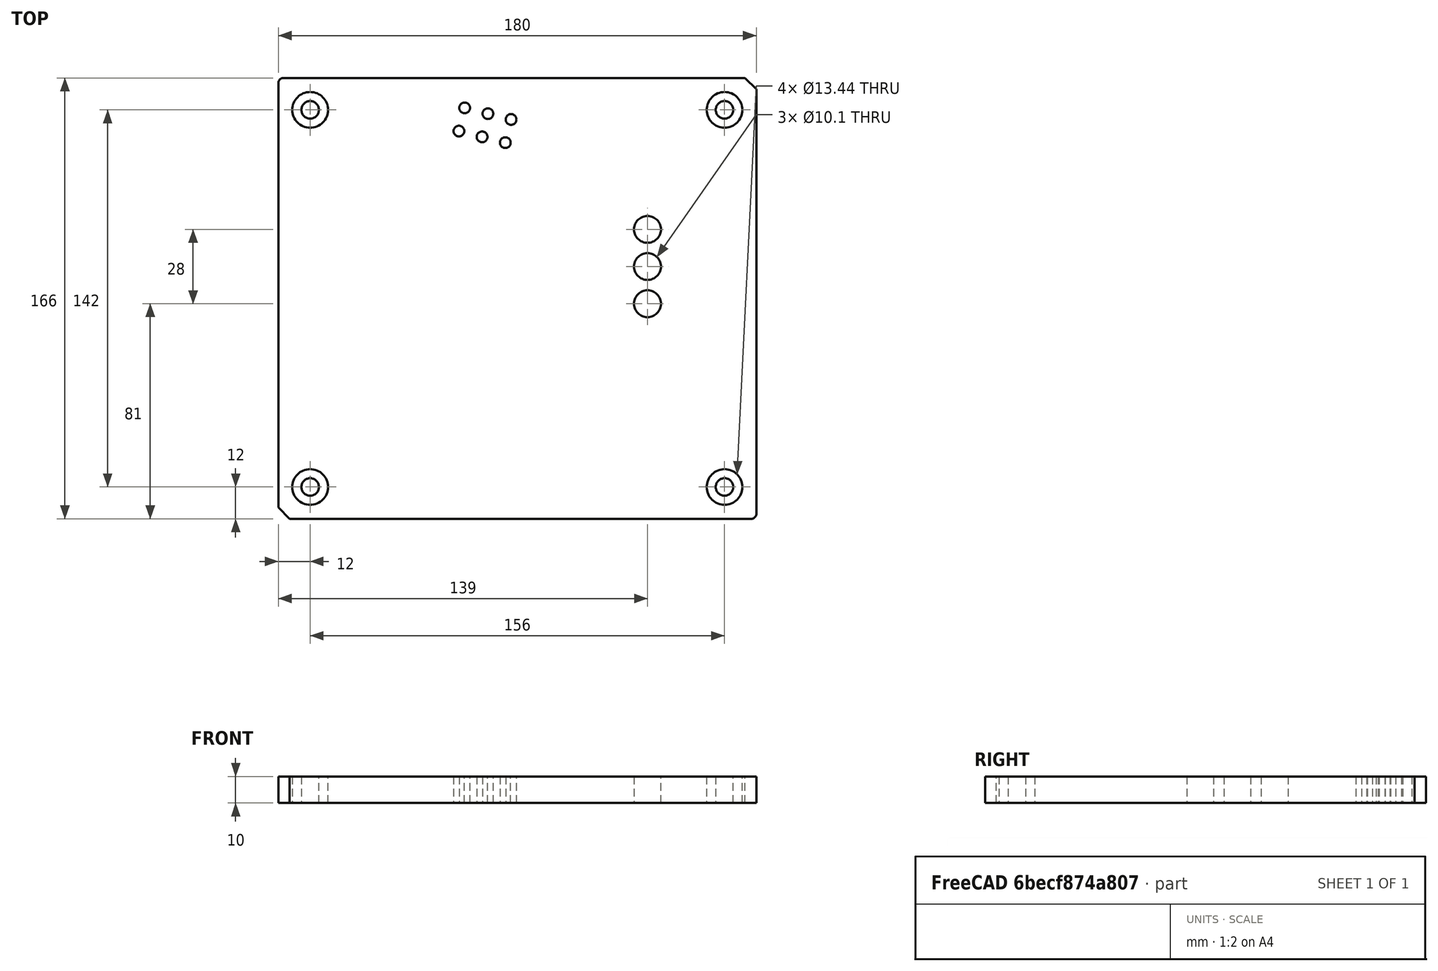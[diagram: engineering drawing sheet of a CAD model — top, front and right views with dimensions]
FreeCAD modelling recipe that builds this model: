
FCSTD DOCUMENT  (FreeCAD 0.19R24348 (Git))
Label: hopefully3d
License: All rights reserved
LicenseURL: http://en.wikipedia.org/wiki/All_rights_reserved
objects: Sketcher::SketchObject×2, Spreadsheet::Sheet×1, Part::Extrusion×1
note: 3 computed .brp shape members not serialized (recipe doc carries the construction recipe); baked Part::Feature solids carry a one-line shape summary decoded from their .brp

FEATURE [Spreadsheet::Sheet] Spreadsheet001  label="Parameters"
  cells = A1=D_1; B1(D_1)=27; A2=KAT; B2(KAT)=14; A3=KAT_2; B3(KAT_2)=28; A4=KPX; B4(KPX)=69; A5=KPY; B5(KPY)=45; A6=D_2; B6(D_2)=39; A7=RKK_1; B7(RKK_1)=6; A8=KOX; B8(KOX)=53; A9=KOY; B9(KOY)=53; A10=WX_1; B10(WX_1)=106; A11=WX_2; B11(WX_2)=136; A12=WY_1; B12(WY_1)=106; A13=RW_1; B13(RW_1)=6; A14=RW_2; B14(RW_2)=14; A15=RW_3; B15(RW_3)=27; A16=RW_4; B16(RW_4)=6; A17=RW_5; B17(RW_5)=6; A18=RW_6; B18(RW_6)=13; A19=FW_1; B19(FW_1)=6; A20=FW_2; B20(FW_2)=5.5; A21=KX_1; B21(KX_1)=12; A22=KX_2; B22(KX_2)=17; A23=KX_3; B23(KX_3)=68; A24=KX_4; B24(KX_4)=139; A25=KX_5; B25(KX_5)=168; A26=KX_6; B26(KX_6)=180; A27=KY_1; B27(KY_1)=12; A28=KY_2; B28(KY_2)=38; A29=KY_3; B29(KY_3)=109; A30=KY_4; B30(KY_4)=146; A31=KY_5; B31(KY_5)=154; A32=KY_6; B32(KY_6)=166; A33=FK_1; B33(FK_1)=2; A34=RK_1; B34(RK_1)=2; A35=H_1; B35(H_1)=12; A36=H_2; B36(H_2)=18; A37=KH_1; B37(KH_1)=10; A38=KH_2; B38(KH_2)=6; A39=OTWX_1; B39(OTWX_1)=9; A40=OTWY_1; B40(OTWY_1)=7; A41=OTWY_2; B41(OTWY_2)=14; A42=GOTW_1; B42(GOTW_1)=14; A43=GOTW_2; B43(GOTW_2)=10; A44=WY_1_1; B44(WY_1_1)=19.0787840283389
FEATURE [Sketcher::SketchObject] Sketch  label="MainFrame"
  FullyConstrained = true
  expr: Constraints[26] = <<Parameters>>.KX_1
  expr: Constraints[29] = <<Parameters>>.KY_6 - <<Parameters>>.KY_5
  expr: Constraints[10] = <<Parameters>>.KY_6
  expr: Constraints[27] = <<Parameters>>.KX_6 - <<Parameters>>.KX_5
  expr: Constraints[9] = <<Parameters>>.KX_6
  expr: Constraints[113] = <<Parameters>>.KAT
  expr: Constraints[47] = <<Parameters>>.FW_1
  expr: Constraints[67] = <<Parameters>>.KX_4
  expr: Constraints[111] = <<Parameters>>.KX_3
  expr: Constraints[68] = <<Parameters>>.KY_3
  expr: Constraints[48] = <<Parameters>>.RK_1
  expr: Constraints[81] = <<Parameters>>.OTWX_1
  expr: Constraints[28] = <<Parameters>>.KY_1
  expr: Constraints[65] = <<Parameters>>.OTWY_2
  expr: Constraints[112] = <<Parameters>>.KY_4
  expr: Constraints[80] = <<Parameters>>.OTWX_1
  sketch-geometry (49):
    g0: LineSegment StartX=0 StartY=0 StartZ=0 EndX=180 EndY=0 EndZ=0
    g1: LineSegment StartX=180 StartY=0 StartZ=0 EndX=180 EndY=166 EndZ=0
    g2: LineSegment StartX=180 StartY=166 StartZ=0 EndX=0 EndY=166 EndZ=0
    g3: LineSegment StartX=0 StartY=166 StartZ=0 EndX=0 EndY=0 EndZ=0
    g4: Circle CenterX=12 CenterY=154 CenterZ=0 NormalX=0 NormalY=0 NormalZ=1 AngleXU=0 Radius=3.3
    g5: Circle CenterX=168 CenterY=154 CenterZ=0 NormalX=0 NormalY=0 NormalZ=1 AngleXU=0 Radius=3.3
    g6: Circle CenterX=168 CenterY=12 CenterZ=0 NormalX=0 NormalY=0 NormalZ=1 AngleXU=0 Radius=3.3
    g7: Circle CenterX=12 CenterY=12 CenterZ=0 NormalX=0 NormalY=0 NormalZ=1 AngleXU=0 Radius=3.3
    g8: LineSegment StartX=12 StartY=154 StartZ=0 EndX=12 EndY=12 EndZ=0
    g9: LineSegment StartX=168 StartY=154 StartZ=0 EndX=12 EndY=154 EndZ=0
    g10: LineSegment StartX=168 StartY=12 StartZ=0 EndX=12 EndY=12 EndZ=0
    g11: LineSegment StartX=168 StartY=154 StartZ=0 EndX=168 EndY=12 EndZ=0
    g12: Circle CenterX=12 CenterY=154 CenterZ=0 NormalX=0 NormalY=0 NormalZ=1 AngleXU=0 Radius=6.72
    g13: Circle CenterX=168 CenterY=154 CenterZ=0 NormalX=0 NormalY=0 NormalZ=1 AngleXU=0 Radius=6.72
    g14: Circle CenterX=168 CenterY=12 CenterZ=0 NormalX=0 NormalY=0 NormalZ=1 AngleXU=0 Radius=6.72
    g15: Circle CenterX=12 CenterY=12 CenterZ=0 NormalX=0 NormalY=0 NormalZ=1 AngleXU=0 Radius=6.72
    g16: ArcOfCircle CenterX=2 CenterY=164 CenterZ=0 NormalX=0 NormalY=0 NormalZ=1 AngleXU=0 Radius=2 StartAngle=1.5708 EndAngle=3.14159
    g17: ArcOfCircle CenterX=178 CenterY=2 CenterZ=0 NormalX=0 NormalY=0 NormalZ=1 AngleXU=0 Radius=2 StartAngle=4.71239 EndAngle=6.28319
    g18: LineSegment StartX=0 StartY=4.24264 StartZ=0 EndX=4.24264 EndY=0 EndZ=0
    g19: LineSegment StartX=175.757 StartY=166 StartZ=0 EndX=180 EndY=161.757 EndZ=0
    g20: LineSegment StartX=0 StartY=4.24264 StartZ=0 EndX=0 EndY=164 EndZ=0
    g21: LineSegment StartX=175.757 StartY=166 StartZ=0 EndX=2 EndY=166 EndZ=0
    g22: LineSegment StartX=180 StartY=161.757 StartZ=0 EndX=180 EndY=2 EndZ=0
    g23: LineSegment StartX=4.24264 StartY=0 StartZ=0 EndX=178 EndY=0 EndZ=0
    g24: Circle CenterX=139 CenterY=109 CenterZ=0 NormalX=0 NormalY=0 NormalZ=1 AngleXU=0 Radius=5.05
    g25: LineSegment StartX=0 StartY=0 StartZ=0 EndX=139 EndY=0 EndZ=0
    g26: Circle CenterX=139 CenterY=95 CenterZ=0 NormalX=0 NormalY=0 NormalZ=1 AngleXU=0 Radius=5.05
    g27: Circle CenterX=139 CenterY=81 CenterZ=0 NormalX=0 NormalY=0 NormalZ=1 AngleXU=0 Radius=5.05
    g28: Circle CenterX=70.1773 CenterY=154.733 CenterZ=0 NormalX=0 NormalY=0 NormalZ=1 AngleXU=0 Radius=2.025
    g29: Circle CenterX=78.91 CenterY=152.555 CenterZ=0 NormalX=0 NormalY=0 NormalZ=1 AngleXU=0 Radius=2.025
    g30: Circle CenterX=87.6426 CenterY=150.378 CenterZ=0 NormalX=0 NormalY=0 NormalZ=1 AngleXU=0 Radius=2.025
    g31: Circle CenterX=68 CenterY=146 CenterZ=0 NormalX=0 NormalY=0 NormalZ=1 AngleXU=0 Radius=2.025
    g32: Circle CenterX=76.7327 CenterY=143.823 CenterZ=0 NormalX=0 NormalY=0 NormalZ=1 AngleXU=0 Radius=2.025
    g33: Circle CenterX=85.4653 CenterY=141.645 CenterZ=0 NormalX=0 NormalY=0 NormalZ=1 AngleXU=0 Radius=2.025
    g34: LineSegment StartX=85.4653 StartY=141.645 StartZ=0 EndX=87.6426 EndY=150.378 EndZ=0
    g35: LineSegment StartX=76.7327 StartY=143.823 StartZ=0 EndX=78.91 EndY=152.555 EndZ=0
    g36: LineSegment StartX=70.1773 StartY=154.733 StartZ=0 EndX=68 EndY=146 EndZ=0
    g37: LineSegment StartX=76.7327 StartY=143.823 StartZ=0 EndX=85.4653 EndY=141.645 EndZ=0
    g38: LineSegment StartX=78.91 StartY=152.555 StartZ=0 EndX=87.6426 EndY=150.378 EndZ=0
    g39: LineSegment StartX=70.1773 StartY=154.733 StartZ=0 EndX=78.91 EndY=152.555 EndZ=0
    g40: LineSegment StartX=68 StartY=146 StartZ=0 EndX=76.7327 EndY=143.823 EndZ=0
    g41: LineSegment StartX=70.1773 StartY=154.733 StartZ=0 EndX=24.9865 EndY=166 EndZ=0
    g42: LineSegment StartX=0 StartY=0 StartZ=0 EndX=68 EndY=0 EndZ=0
    g43: LineSegment StartX=68 StartY=0 StartZ=0 EndX=68 EndY=146 EndZ=0
    g44: LineSegment StartX=68 StartY=146 StartZ=0 EndX=0 EndY=146 EndZ=0
    g45: LineSegment StartX=0 StartY=146 StartZ=0 EndX=0 EndY=0 EndZ=0
    g46: LineSegment StartX=139 StartY=81 StartZ=0 EndX=139 EndY=95 EndZ=0
    g47: LineSegment StartX=139 StartY=109 StartZ=0 EndX=139 EndY=95 EndZ=0
    g48: LineSegment StartX=139 StartY=0 StartZ=0 EndX=139 EndY=81 EndZ=0
  constraints (124):
    c: Coincident(g0,g1)
    c: Coincident(g1,g2)
    c: Coincident(g2,g3)
    c: Coincident(g3,g0)
    c: Horizontal(g0)
    c: Horizontal(g2)
    c: Vertical(g1)
    c: Vertical(g3)
    c: Coincident(g0,g-1)
    c: DistanceX(g0,g0) = 180
    c: DistanceY(g3,g3) = 166
    c: Equal(g5,g4)
    c: Equal(g4,g7)
    c: Equal(g7,g6)
    c: Coincident(g8,g4)
    c: Coincident(g8,g7)
    c: Vertical(g8)
    c: Coincident(g9,g5)
    c: Coincident(g9,g4)
    c: Horizontal(g9)
    c: Coincident(g10,g6)
    c: Coincident(g10,g7)
    c: Horizontal(g10)
    c: Coincident(g11,g5)
    c: Coincident(g11,g6)
    c: Vertical(g11)
    c: DistanceX(g-1,g7) = 12
    c: DistanceX(g6,g0) = 12
    c: DistanceY(g-1,g7) = 12
    c: DistanceY(g4,g2) = 12
    c: Coincident(g12,g4)
    c: Coincident(g13,g5)
    c: Coincident(g14,g6)
    c: Coincident(g15,g7)
    c: Equal(g15,g12)
    c: Equal(g12,g13)
    c: Equal(g13,g14)
    c: Diameter(g4) = 6.6
    c: Diameter(g12) = 13.44
    c: PointOnObject(g18,g3)
    c: PointOnObject(g18,g0)
    c: PointOnObject(g19,g2)
    c: PointOnObject(g19,g1)
    c: Equal(g16,g17)
    c: Equal(g18,g19)
    c: Angle(g18,g3) = 2.35619
    c: Angle(g2,g19) = 2.35619
    c: Distance(g19) = 6
    c: Radius(g17) = 2
    c: Tangent(g17,g0) = -1.5708
    c: Tangent(g17,g1) = -1.5708
    c: Tangent(g16,g2) = -1.5708
    c: Tangent(g16,g3) = -1.5708
    c: Coincident(g20,g18)
    c: Coincident(g20,g16)
    c: Coincident(g21,g19)
    c: Coincident(g21,g16)
    c: Coincident(g22,g19)
    c: Coincident(g22,g17)
    c: Coincident(g23,g18)
    c: Coincident(g23,g17)
    c: Horizontal(g25)
    c: Coincident(g25,g-1)
    c: Equal(g27,g26)
    c: Equal(g26,g24)
    c: DistanceY(g26,g24) = 14
    c: Radius(g24) = 5.05
    c: DistanceX(g-1,g24) = 139
    c: DistanceY(g-1,g24) = 109
    c: Equal(g28,g31)
    c: Equal(g31,g29)
    c: Equal(g29,g32)
    c: Equal(g32,g33)
    c: Equal(g33,g30)
    c: Coincident(g34,g33)
    c: Coincident(g34,g30)
    c: Coincident(g35,g32)
    c: Coincident(g35,g29)
    c: Coincident(g36,g28)
    c: Coincident(g36,g31)
    c: Distance(g28,g29) = 9
    c: Distance(g34) = 9
    c: Coincident(g37,g32)
    c: Coincident(g37,g33)
    c: Coincident(g38,g29)
    c: Coincident(g38,g30)
    c: Coincident(g39,g28)
    c: Coincident(g39,g29)
    c: Coincident(g40,g31)
    c: Coincident(g40,g32)
    c: Equal(g39,g40)
    c: Equal(g40,g37)
    c: Equal(g37,g38)
    c: Perpendicular(g38,g35)
    c: Perpendicular(g35,g39)
    c: Perpendicular(g40,g36)
    c: Perpendicular(g35,g37)
    c: Diameter(g29) = 4.05
    c: Coincident(g41,g28)
    c: Parallel(g41,g40)
    c: PointOnObject(g41,g21)
    c: Coincident(g42,g43)
    c: Coincident(g43,g44)
    c: Coincident(g44,g45)
    c: Coincident(g45,g42)
    c: Horizontal(g42)
    c: Horizontal(g44)
    c: Vertical(g43)
    c: Vertical(g45)
    c: Coincident(g42,g-1)
    c: Coincident(g43,g31)
    c: DistanceX(g44,g44) = 68
    c: DistanceY(g43,g43) = 146
    c: Angle(g41,g21) = 0.244346
    c: Coincident(g46,g27)
    c: Coincident(g46,g26)
    c: Vertical(g46)
    c: Coincident(g47,g24)
    c: Coincident(g47,g26)
    c: Vertical(g47)
    c: Coincident(g48,g25)
    c: Coincident(g48,g27)
    c: Vertical(g48)
    c: Equal(g47,g46)
FEATURE [Part::Extrusion] Extrude
  Base = -> Sketch
  Dir = (0,0,1)
  DirMode = 2
  FaceMakerClass = Part::FaceMakerBullseye
  LengthFwd = 10
  LengthRev = 0
  Solid = true
  Symmetric = false
FEATURE [Sketcher::SketchObject] Sketch001  label="MiddleFrame"
  FullyConstrained = true
  MapMode = 2
  expr: Constraints[142] = <<Parameters>>.RW_3
  expr: Constraints[93] = <<Parameters>>.D_2
  expr: Constraints[30] = <<Parameters>>.WX_1
  expr: Constraints[31] = <<Parameters>>.WY_1
  expr: Constraints[101] = <<Parameters>>.KPX
  expr: Constraints[112] = <<Parameters>>.RKK_1
  expr: Constraints[36] = <<Parameters>>.RW_6
  expr: Constraints[102] = <<Parameters>>.KPY
  expr: Constraints[143] = <<Parameters>>.RW_4
  expr: Constraints[58] = <<Parameters>>.WX_2 - <<Parameters>>.WX_1
  expr: Constraints[71] = <<Parameters>>.KOX
  expr: Constraints[15] = <<Parameters>>.KX_2
  expr: Constraints[33] = <<Parameters>>.RW_2
  expr: Constraints[70] = <<Parameters>>.KOY
  expr: Constraints[141] = <<Parameters>>.KAT_2
  expr: Constraints[14] = <<Parameters>>.KY_2
  expr: Constraints[92] = <<Parameters>>.D_1
  expr: Constraints[57] = <<Parameters>>.FW_2
  expr: Constraints[32] = <<Parameters>>.RW_1
  expr: Constraints[26] = 90 + <<Parameters>>.KAT
  expr: Constraints[37] = <<Parameters>>.RW_5
  expr: Constraints[35] = <<Parameters>>.FW_1
  sketch-geometry (57):
    g0: LineSegment StartX=0 StartY=0 StartZ=0 EndX=17 EndY=0 EndZ=0
    g1: LineSegment StartX=17 StartY=0 StartZ=0 EndX=17 EndY=38 EndZ=0
    g2: LineSegment StartX=17 StartY=38 StartZ=0 EndX=0 EndY=38 EndZ=0
    g3: LineSegment StartX=0 StartY=38 StartZ=0 EndX=0 EndY=0 EndZ=0
    g4: LineSegment StartX=17 StartY=38 StartZ=0 EndX=119.851 EndY=12.3563 EndZ=0
    g5: LineSegment StartX=119.851 StartY=12.3563 StartZ=0 EndX=145.495 EndY=115.208 EndZ=0
    g6: LineSegment StartX=145.495 StartY=115.208 StartZ=0 EndX=42.6437 EndY=140.851 EndZ=0
    g7: LineSegment StartX=42.6437 StartY=140.851 StartZ=0 EndX=17 EndY=38 EndZ=0
    g8: LineSegment StartX=18.0264 StartY=42.1166 StartZ=0 EndX=21.1166 EndY=36.9736 EndZ=0
    g9: ArcOfCircle CenterX=42.6437 CenterY=140.851 CenterZ=0 NormalX=0 NormalY=0 NormalZ=1 AngleXU=0 Radius=14 StartAngle=0.0603466 EndAngle=4.16335
    g10: ArcOfCircle CenterX=122.996 CenterY=24.9701 CenterZ=0 NormalX=0 NormalY=0 NormalZ=1 AngleXU=0 Radius=13 StartAngle=4.46804 EndAngle=6.03884
    g11: ArcOfCircle CenterX=141.432 CenterY=20.3736 CenterZ=0 NormalX=0 NormalY=0 NormalZ=1 AngleXU=0 Radius=6 StartAngle=1.32645 EndAngle=2.89725
    g12: ArcOfCircle CenterX=32.2064 CenterY=123.791 CenterZ=0 NormalX=0 NormalY=0 NormalZ=1 AngleXU=0 Radius=6 StartAngle=6.03884 EndAngle=7.30494
    g13: ArcOfCircle CenterX=62.6073 CenterY=142.058 CenterZ=0 NormalX=0 NormalY=0 NormalZ=1 AngleXU=0 Radius=6 StartAngle=3.20194 EndAngle=4.46804
    g14: LineSegment StartX=38.0281 StartY=122.339 StartZ=0 EndX=18.0264 EndY=42.1166 EndZ=0
    g15: LineSegment StartX=122.996 StartY=24.9701 StartZ=0 EndX=141.432 EndY=20.3736 EndZ=0
    g16: LineSegment StartX=119.851 StartY=12.3563 StartZ=0 EndX=148.96 EndY=5.09862 EndZ=0
    g17: LineSegment StartX=174.604 StartY=107.95 StartZ=0 EndX=148.96 EndY=5.09862 EndZ=0
    g18: LineSegment StartX=142.883 StartY=26.1954 StartZ=0 EndX=153.557 EndY=23.5342 EndZ=0
    g19: LineSegment StartX=149.783 StartY=24.4751 StartZ=0 EndX=154.498 EndY=27.3078 EndZ=0
    g20: LineSegment StartX=149.783 StartY=24.4751 StartZ=0 EndX=142.883 EndY=26.1954 EndZ=0
    g21: LineSegment StartX=145.495 StartY=115.208 StartZ=0 EndX=174.604 EndY=107.95 EndZ=0
    g22: LineSegment StartX=145.495 StartY=115.208 StartZ=0 EndX=61.1558 EndY=136.236 EndZ=0
    g23: LineSegment StartX=21.1166 StartY=36.9736 StartZ=0 EndX=119.851 EndY=12.3563 EndZ=0
    g24: LineSegment StartX=29.8219 StartY=89.4257 StartZ=0 EndX=81.2475 EndY=76.6038 EndZ=0
    g25: LineSegment StartX=81.2475 StartY=76.6038 StartZ=0 EndX=68.4257 EndY=25.1781 EndZ=0
    g26: Circle CenterX=81.2475 CenterY=76.6038 CenterZ=0 NormalX=0 NormalY=0 NormalZ=1 AngleXU=0 Radius=13.5
    g27: Circle CenterX=81.2475 CenterY=76.6038 CenterZ=0 NormalX=0 NormalY=0 NormalZ=1 AngleXU=0 Radius=19.5
    g28: Circle CenterX=64.5328 CenterY=86.6471 CenterZ=0 NormalX=0 NormalY=0 NormalZ=1 AngleXU=0 Radius=2.525
    g29: Circle CenterX=91.2908 CenterY=93.3186 CenterZ=0 NormalX=0 NormalY=0 NormalZ=1 AngleXU=0 Radius=2.525
    g30: Circle CenterX=97.9623 CenterY=66.5606 CenterZ=0 NormalX=0 NormalY=0 NormalZ=1 AngleXU=0 Radius=2.525
    g31: Circle CenterX=71.2043 CenterY=59.8891 CenterZ=0 NormalX=0 NormalY=0 NormalZ=1 AngleXU=0 Radius=2.525
    g32: LineSegment StartX=71.2043 StartY=59.8891 StartZ=0 EndX=81.2475 EndY=76.6038 EndZ=0
    g33: LineSegment StartX=64.5328 StartY=86.6471 StartZ=0 EndX=81.2475 EndY=76.6038 EndZ=0
    g34: LineSegment StartX=91.2908 StartY=93.3186 StartZ=0 EndX=81.2475 EndY=76.6038 EndZ=0
    g35: LineSegment StartX=97.9623 StartY=66.5606 StartZ=0 EndX=81.2475 EndY=76.6038 EndZ=0
    g36: LineSegment StartX=42.3291 StartY=90.0892 StartZ=0 EndX=109.279 EndY=106.782 EndZ=0
    g37: LineSegment StartX=109.279 StartY=106.782 StartZ=0 EndX=120.166 EndY=63.1185 EndZ=0
    g38: LineSegment StartX=120.166 StartY=63.1185 StartZ=0 EndX=53.2156 EndY=46.4259 EndZ=0
    g39: LineSegment StartX=53.2156 StartY=46.4259 StartZ=0 EndX=42.3291 EndY=90.0892 EndZ=0
    g40: LineSegment StartX=81.2475 StartY=76.6038 StartZ=0 EndX=75.8043 EndY=98.4355 EndZ=0
    g41: LineSegment StartX=47.7723 StartY=68.2575 StartZ=0 EndX=81.2475 EndY=76.6038 EndZ=0
    g42: ArcOfCircle CenterX=49.6024 CenterY=85.7189 CenterZ=0 NormalX=0 NormalY=0 NormalZ=1 AngleXU=0 Radius=6 StartAngle=1.81514 EndAngle=3.38594
    g43: ArcOfCircle CenterX=104.909 CenterY=99.5085 CenterZ=0 NormalX=0 NormalY=0 NormalZ=1 AngleXU=0 Radius=6 StartAngle=0.244346 EndAngle=1.81514
    g44: ArcOfCircle CenterX=112.893 CenterY=67.4887 CenterZ=0 NormalX=0 NormalY=0 NormalZ=1 AngleXU=0 Radius=6 StartAngle=4.95674 EndAngle=6.52753
    g45: ArcOfCircle CenterX=57.5858 CenterY=53.6992 CenterZ=0 NormalX=0 NormalY=0 NormalZ=1 AngleXU=0 Radius=6 StartAngle=3.38594 EndAngle=4.95674
    g46: LineSegment StartX=51.764 StartY=52.2476 StartZ=0 EndX=43.7806 EndY=84.2674 EndZ=0
    g47: LineSegment StartX=48.1509 StartY=91.5407 StartZ=0 EndX=103.458 EndY=105.33 EndZ=0
    g48: LineSegment StartX=110.731 StartY=100.96 StartZ=0 EndX=118.714 EndY=68.9402 EndZ=0
    g49: LineSegment StartX=114.344 StartY=61.6669 StartZ=0 EndX=59.0373 EndY=47.8774 EndZ=0
    g50: LineSegment StartX=81.2475 StartY=76.6038 StartZ=0 EndX=114.723 EndY=84.9501 EndZ=0
    g51: LineSegment StartX=81.2475 StartY=76.6038 StartZ=0 EndX=86.6908 EndY=54.7722 EndZ=0
    g52: LineSegment StartX=64.5328 StartY=86.6471 StartZ=0 EndX=91.2908 EndY=93.3186 EndZ=0
    g53: ArcOfCircle CenterX=138.963 CenterY=89.0096 CenterZ=0 NormalX=0 NormalY=0 NormalZ=1 AngleXU=0 Radius=27 StartAngle=0.830867 EndAngle=1.32645
    g54: ArcOfCircle CenterX=164.887 CenterY=93.7779 CenterZ=0 NormalX=0 NormalY=0 NormalZ=1 AngleXU=0 Radius=6 StartAngle=6.03884 EndAngle=7.11405
    g55: LineSegment StartX=157.168 StartY=108.95 StartZ=0 EndX=168.932 EndY=98.2089 EndZ=0
    g56: LineSegment StartX=170.709 StartY=92.3263 StartZ=0 EndX=154.498 EndY=27.3078 EndZ=0
  constraints (154):
    c: Coincident(g0,g1)
    c: Coincident(g1,g2)
    c: Coincident(g2,g3)
    c: Coincident(g3,g0)
    c: Horizontal(g0)
    c: Horizontal(g2)
    c: Vertical(g1)
    c: Vertical(g3)
    c: Coincident(g0,g-1)
    c: Coincident(g4,g5)
    c: Coincident(g5,g6)
    c: Coincident(g6,g7)
    c: Coincident(g7,g4)
    c: Coincident(g4,g1)
    c: DistanceY(g3,g3) = 38
    c: DistanceX(g0,g0) = 17
    c: PointOnObject(g8,g7)
    c: PointOnObject(g8,g4)
    c: Coincident(g9,g6)
    c: Equal(g13,g12)
    c: Tangent(g12,g7) = 1.5708
    c: Tangent(g9,g12) = 1.5708
    c: Tangent(g13,g9) = 1.5708
    c: Tangent(g13,g6) = 1.5708
    c: Coincident(g14,g12)
    c: Coincident(g14,g8)
    c: Angle(g7,g2) = 1.81514
    c: Perpendicular(g14,g4)
    c: Perpendicular(g4,g5)
    c: Perpendicular(g6,g7)
    c: Distance(g4) = 106
    c: Distance(g9,g1) = 106
    c: Radius(g12) = 6
    c: Radius(g9) = 14
    c: Angle(g8,g7) = 2.35619
    c: Distance(g8) = 6
    c: Radius(g10) = 13
    c: Radius(g11) = 6
    c: Coincident(g15,g10)
    c: Coincident(g15,g11)
    c: Parallel(g15,g4)
    c: Tangent(g11,g10) = 1.5708
    c: Coincident(g16,g4)
    c: Coincident(g17,g16)
    c: Parallel(g17,g5)
    c: Coincident(g10,g4)
    c: Tangent(g10,g16)
    c: Parallel(g16,g4)
    c: Coincident(g18,g11)
    c: PointOnObject(g18,g17)
    c: Perpendicular(g17,g18)
    c: Tangent(g11,g18)
    c: PointOnObject(g19,g18)
    c: PointOnObject(g19,g17)
    c: Coincident(g20,g19)
    c: Coincident(g20,g11)
    c: Angle(g17,g19) = 2.35619
    c: Distance(g19) = 5.5
    c: Distance(g10,g16) = 30
    c: Coincident(g21,g5)
    c: Coincident(g21,g17)
    c: Parallel(g21,g16)
    c: Coincident(g22,g13)
    c: Coincident(g23,g8)
    c: Coincident(g23,g10)
    c: PointOnObject(g24,g14)
    c: Coincident(g25,g24)
    c: PointOnObject(g25,g23)
    c: Perpendicular(g25,g24)
    c: Perpendicular(g24,g14)
    c: Distance(g24) = 53
    c: Distance(g25) = 53
    c: Coincident(g26,g24)
    c: Coincident(g27,g26)
    c: PointOnObject(g28,g27)
    c: PointOnObject(g29,g27)
    c: PointOnObject(g30,g27)
    c: PointOnObject(g31,g27)
    c: Equal(g28,g31)
    c: Equal(g31,g30)
    c: Equal(g30,g29)
    c: Coincident(g32,g31)
    c: Coincident(g32,g26)
    c: Coincident(g33,g28)
    c: Coincident(g33,g26)
    c: Coincident(g34,g29)
    c: Coincident(g34,g26)
    c: Coincident(g35,g30)
    c: Coincident(g35,g26)
    c: Angle(g33,g32) = 1.5708
    c: Angle(g34,g33) = 1.5708
    c: Angle(g35,g34) = 1.5708
    c: Diameter(g26) = 27
    c: Diameter(g27) = 39
    c: Coincident(g37,g36)
    c: Coincident(g38,g37)
    c: Coincident(g39,g36)
    c: Coincident(g39,g38)
    c: Perpendicular(g36,g39)
    c: Perpendicular(g36,g37)
    c: Perpendicular(g39,g38)
    c: Distance(g36) = 69
    c: Distance(g39) = 45
    c: Coincident(g40,g26)
    c: PointOnObject(g40,g36)
    c: PointOnObject(g41,g39)
    c: Coincident(g41,g26)
    c: Perpendicular(g39,g41)
    c: Perpendicular(g36,g40)
    c: Equal(g45,g42)
    c: Equal(g42,g43)
    c: Equal(g43,g44)
    c: Radius(g44) = 6
    c: Tangent(g42,g36) = 1.5708
    c: Tangent(g43,g37) = 1.5708
    c: Tangent(g43,g36) = 1.5708
    c: Tangent(g42,g39) = 1.5708
    c: Tangent(g44,g38) = 1.5708
    c: Tangent(g44,g37) = 1.5708
    c: Tangent(g45,g39) = 1.5708
    c: Tangent(g45,g38) = 1.5708
    c: Coincident(g46,g45)
    c: Coincident(g46,g42)
    c: Coincident(g47,g42)
    c: Coincident(g47,g43)
    c: Coincident(g48,g43)
    c: Coincident(g48,g44)
    c: Coincident(g49,g44)
    c: Coincident(g49,g45)
    c: Coincident(g50,g26)
    c: PointOnObject(g50,g48)
    c: Perpendicular(g48,g50)
    c: Coincident(g51,g26)
    c: PointOnObject(g51,g49)
    c: Perpendicular(g51,g49)
    c: Equal(g50,g41)
    c: Equal(g40,g51)
    c: Coincident(g52,g28)
    c: Parallel(g52,g49)
    c: Coincident(g52,g29)
    c: Diameter(g30) = 5.05
    c: Angle(g23,g49) = 0.488692
    c: Radius(g53) = 27
    c: Radius(g54) = 6
    c: PointOnObject(g22,g53)
    c: Tangent(g22,g53)
    c: Coincident(g22,g5)
    c: PointOnObject(g53,g5)
    c: Tangent(g53,g55) = 1.5708
    c: Tangent(g54,g55) = 1.5708
    c: Tangent(g54,g17) = 1.5708
    c: Coincident(g56,g54)
    c: Coincident(g56,g19)
    c: Tangent(g53,g21)
